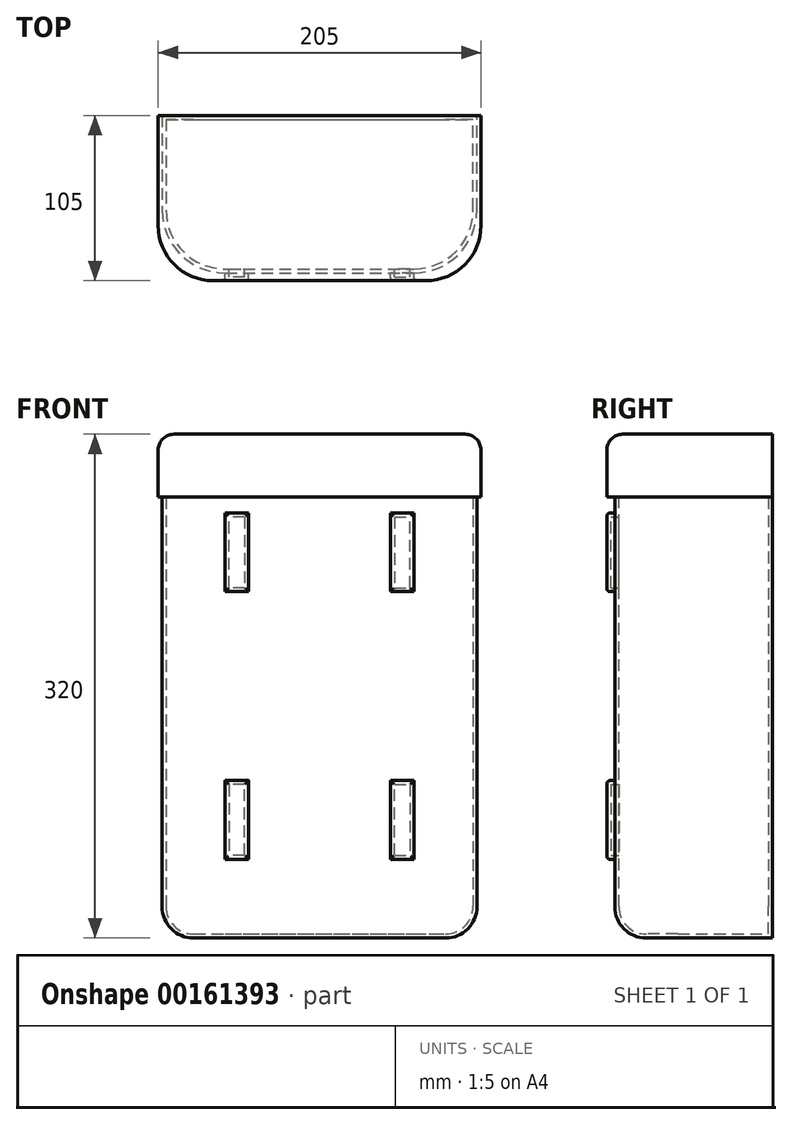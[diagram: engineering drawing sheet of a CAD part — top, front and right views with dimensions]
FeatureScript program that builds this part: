
annotation { "Feature Type Name" : "Feature", "Feature Type Description" : "" }
export const myFeature = defineFeature(function(context is Context, id is Id, definition is map)
    precondition{}
    {
        {
            var Q0;
            Q0=qCreatedBy(makeId("Top.planeOp"),FACE);
            var sketch = newSketch(context, id + "F0", { "sketchPlane" : qUnion([Q0])});
            skLineSegment(sketch, "E0.bottom", {"start": v(-100.73, 42.4) * mm, "end": v(-0.73, 42.4) * mm});
            skLineSegment(sketch, "E0.top", {"start": v(-100.73, -57.6) * mm, "end": v(-0.73, -57.6) * mm});
            skLineSegment(sketch, "E0.left", {"start": v(-100.73, 42.4) * mm, "end": v(-100.73, -57.6) * mm});
            skLineSegment(sketch, "E0.right", {"start": v(-0.73, 42.4) * mm, "end": v(-0.73, -57.6) * mm});
            skSolve(sketch);
        }
        {
            var Q0;
            Q0 = qSketchRegion(id + "F0", true);
            extrude(context, id + "F1", {"entities" : qUnion([Q0]), "depth" : 160 * mm});
        }
        {
            var Q0;
            {var subQ0=makeQuery(id+"F1.opExtrude","SWEPT_FACE",FACE,{"disambiguationData":[OSD([sQuery(id+"F0.wireOp",EDGE,"E0.top")])]});Q0=makeQuery(id+"FtQzAAAF3xHTHlU_1.boolean.opBoolean","MERGE",FACE,{"derivedFrom":[subQ0,makeQuery(id+"FtQzAAAF3xHTHlU_1.opPattern","COPY",FACE,{"derivedFrom":subQ0,"instanceName":"1"})]});}
            var sketch = newSketch(context, id + "F2", { "sketchPlane" : qUnion([Q0])});
            skLineSegment(sketch, "E1.bottom", {"start": v(-60.73, 100) * mm, "end": v(-45.73, 100) * mm});
            skLineSegment(sketch, "E1.top", {"start": v(-60.73, 50) * mm, "end": v(-45.73, 50) * mm});
            skLineSegment(sketch, "E1.left", {"start": v(-60.73, 100) * mm, "end": v(-60.73, 50) * mm});
            skLineSegment(sketch, "E1.right", {"start": v(-45.73, 100) * mm, "end": v(-45.73, 50) * mm});
            skSolve(sketch);
        }
        {
            var Q0;
            Q0 = qSketchRegion(id + "F2", true);
            extrude(context, id + "F3", {"entities" : qUnion([Q0]), "operationType" : NewBodyOperationType.ADD, "depth" : 5 * mm});
        }
        {
            var Q0;
            Q0=makeQuery(id+"F1.opExtrude","SWEPT_BODY",BODY,{"disambiguationData":[OSD([sQuery(id+"F0.wireOp",EDGE,"E0.bottom"),sQuery(id+"F0.wireOp",EDGE,"E0.top"),sQuery(id+"F0.wireOp",EDGE,"E0.left"),sQuery(id+"F0.wireOp",EDGE,"E0.right")])]});
            var Q1;
            Q1=makeQuery(id+"F1.opExtrude","SWEPT_FACE",FACE,{"disambiguationData":[OSD([sQuery(id+"F0.wireOp",EDGE,"E0.right")])]});
            mirror(context, id + "F4", {"operationType" : NewBodyOperationType.ADD, "entities" : qUnion([Q0]), "mirrorPlane" : qUnion([Q1])});
        }
        {
            var Q0;
            Q0=makeQuery(id+"F1.opExtrude","SWEPT_BODY",BODY,{"disambiguationData":[OSD([sQuery(id+"F0.wireOp",EDGE,"E0.bottom"),sQuery(id+"F0.wireOp",EDGE,"E0.top"),sQuery(id+"F0.wireOp",EDGE,"E0.left"),sQuery(id+"F0.wireOp",EDGE,"E0.right")])]});
            var Q1;
            {var subQ0=makeQuery(id+"F1.opExtrude","CAP_FACE",FACE,{"disambiguationData":[OSD([sQuery(id+"F0.wireOp",EDGE,"E0.bottom"),sQuery(id+"F0.wireOp",EDGE,"E0.top"),sQuery(id+"F0.wireOp",EDGE,"E0.left"),sQuery(id+"F0.wireOp",EDGE,"E0.right")])],"isStart":false});Q1=makeQuery(id+"F4.boolean.opBoolean","MERGE",FACE,{"derivedFrom":[subQ0,makeQuery(id+"F4.opPattern","COPY",FACE,{"derivedFrom":subQ0,"instanceName":"1"})]});}
            mirror(context, id + "F5", {"operationType" : NewBodyOperationType.ADD, "entities" : qUnion([Q0]), "mirrorPlane" : qUnion([Q1])});
        }
        {
            var Q0;
            Q0=makeQuery(id+"F5.opPattern","COPY",FACE,{"derivedFrom":makeQuery(id+"F3.opExtrude","CAP_FACE",FACE,{"disambiguationData":[OSD([sQuery(id+"F2.wireOp",EDGE,"E1.bottom"),sQuery(id+"F2.wireOp",EDGE,"E1.top"),sQuery(id+"F2.wireOp",EDGE,"E1.left"),sQuery(id+"F2.wireOp",EDGE,"E1.right")])],"isStart":false}),"instanceName":"1"});
            fillet(context, id + "F6", {"entities" : qUnion([Q0]), "radius" : 2 * mm, "tangentPropagation" : true, "allowEdgeOverflow" : false});
        }
        {
            var Q0;
            Q0=makeQuery(id+"F5.opPattern","COPY",FACE,{"derivedFrom":makeQuery(id+"F4.opPattern","COPY",FACE,{"derivedFrom":makeQuery(id+"F3.opExtrude","CAP_FACE",FACE,{"disambiguationData":[OSD([sQuery(id+"F2.wireOp",EDGE,"E1.bottom"),sQuery(id+"F2.wireOp",EDGE,"E1.top"),sQuery(id+"F2.wireOp",EDGE,"E1.left"),sQuery(id+"F2.wireOp",EDGE,"E1.right")])],"isStart":false}),"instanceName":"1"}),"instanceName":"1"});
            fillet(context, id + "F7", {"entities" : qUnion([Q0]), "radius" : 2 * mm, "tangentPropagation" : true, "allowEdgeOverflow" : false});
        }
        {
            var Q0;
            Q0=makeQuery(id+"F3.opExtrude","CAP_FACE",FACE,{"disambiguationData":[OSD([sQuery(id+"F2.wireOp",EDGE,"E1.bottom"),sQuery(id+"F2.wireOp",EDGE,"E1.top"),sQuery(id+"F2.wireOp",EDGE,"E1.left"),sQuery(id+"F2.wireOp",EDGE,"E1.right")])],"isStart":false});
            var Q1;
            Q1=makeQuery(id+"F4.opPattern","COPY",FACE,{"derivedFrom":makeQuery(id+"F3.opExtrude","CAP_FACE",FACE,{"disambiguationData":[OSD([sQuery(id+"F2.wireOp",EDGE,"E1.bottom"),sQuery(id+"F2.wireOp",EDGE,"E1.top"),sQuery(id+"F2.wireOp",EDGE,"E1.left"),sQuery(id+"F2.wireOp",EDGE,"E1.right")])],"isStart":false}),"instanceName":"1"});
            fillet(context, id + "F8", {"entities" : qUnion([Q0, Q1]), "radius" : 2 * mm, "tangentPropagation" : true, "allowEdgeOverflow" : false});
        }
        {
            var Q0;
            {var subQ0=makeQuery(id+"F1.opExtrude","SWEPT_EDGE",EDGE,{"disambiguationData":[OSD([sQuery(id+"F0.wireOp",EDGE,"E0.top"),sQuery(id+"F0.wireOp",EDGE,"E0.left")])]});Q0=makeQuery(id+"F5.boolean.opBoolean","MERGE",EDGE,{"derivedFrom":[subQ0,makeQuery(id+"F5.opPattern","COPY",EDGE,{"derivedFrom":subQ0,"instanceName":"1"})]});}
            fillet(context, id + "F9", {"entities" : qUnion([Q0]), "radius" : 40 * mm, "tangentPropagation" : true, "allowEdgeOverflow" : false});
        }
        {
            var Q0;
            {var subQ0=makeQuery(id+"F4.opPattern","COPY",EDGE,{"derivedFrom":makeQuery(id+"F1.opExtrude","SWEPT_EDGE",EDGE,{"disambiguationData":[OSD([sQuery(id+"F0.wireOp",EDGE,"E0.top"),sQuery(id+"F0.wireOp",EDGE,"E0.left")])]}),"instanceName":"1"});Q0=makeQuery(id+"F5.boolean.opBoolean","MERGE",EDGE,{"derivedFrom":[subQ0,makeQuery(id+"F5.opPattern","COPY",EDGE,{"derivedFrom":subQ0,"instanceName":"1"})]});}
            fillet(context, id + "F10", {"entities" : qUnion([Q0]), "radius" : 40 * mm, "tangentPropagation" : true, "allowEdgeOverflow" : false});
        }
        {
            var Q0;
            {var subQ0=sQuery(id+"F0.wireOp",EDGE,"E0.left");var subQ1=sQuery(id+"F0.wireOp",EDGE,"E0.top");var subQ2=makeQuery(id+"F1.opExtrude","CAP_FACE",FACE,{"disambiguationData":[OSD([sQuery(id+"F0.wireOp",EDGE,"E0.bottom"),subQ1,subQ0,sQuery(id+"F0.wireOp",EDGE,"E0.right")])],"isStart":true});var subQ3=makeQuery(id+"F1.opExtrude","SWEPT_EDGE",EDGE,{"disambiguationData":[OSD([subQ1,subQ0])]});Q0=makeQuery(id+"F9.opFillet","BLEND_EDGE",EDGE,{"blendedFrom":[makeQuery(id+"F5.boolean.opBoolean","MERGE",EDGE,{"derivedFrom":[subQ3,makeQuery(id+"F5.opPattern","COPY",EDGE,{"derivedFrom":subQ3,"instanceName":"1"})]}),makeQuery(id+"F4.boolean.opBoolean","MERGE",FACE,{"derivedFrom":[subQ2,makeQuery(id+"F4.opPattern","COPY",FACE,{"derivedFrom":subQ2,"instanceName":"1"})]})],"blendedInto":[makeQuery(id+"F4.boolean.opBoolean","MERGE",FACE,{"derivedFrom":[subQ2,makeQuery(id+"F4.opPattern","COPY",FACE,{"derivedFrom":subQ2,"instanceName":"1"})]})]});}
            var Q1;
            {var subQ0=sQuery(id+"F0.wireOp",EDGE,"E0.left");var subQ1=sQuery(id+"F0.wireOp",EDGE,"E0.top");var subQ2=makeQuery(id+"F1.opExtrude","CAP_FACE",FACE,{"disambiguationData":[OSD([sQuery(id+"F0.wireOp",EDGE,"E0.bottom"),subQ1,subQ0,sQuery(id+"F0.wireOp",EDGE,"E0.right")])],"isStart":true});var subQ3=makeQuery(id+"F4.opPattern","COPY",EDGE,{"derivedFrom":makeQuery(id+"F1.opExtrude","SWEPT_EDGE",EDGE,{"disambiguationData":[OSD([subQ1,subQ0])]}),"instanceName":"1"});Q1=makeQuery(id+"F10.opFillet","BLEND_EDGE",EDGE,{"blendedFrom":[makeQuery(id+"F5.boolean.opBoolean","MERGE",EDGE,{"derivedFrom":[subQ3,makeQuery(id+"F5.opPattern","COPY",EDGE,{"derivedFrom":subQ3,"instanceName":"1"})]}),makeQuery(id+"F4.boolean.opBoolean","MERGE",FACE,{"derivedFrom":[subQ2,makeQuery(id+"F4.opPattern","COPY",FACE,{"derivedFrom":subQ2,"instanceName":"1"})]})],"blendedInto":[makeQuery(id+"F4.boolean.opBoolean","MERGE",FACE,{"derivedFrom":[subQ2,makeQuery(id+"F4.opPattern","COPY",FACE,{"derivedFrom":subQ2,"instanceName":"1"})]})]});}
            fillet(context, id + "F11", {"entities" : qUnion([Q0, Q1]), "radius" : 20 * mm, "tangentPropagation" : true, "allowEdgeOverflow" : false});
        }
        {
            var Q0;
            {var subQ0=makeQuery(id+"F1.opExtrude","CAP_FACE",FACE,{"disambiguationData":[OSD([sQuery(id+"F0.wireOp",EDGE,"E0.bottom"),sQuery(id+"F0.wireOp",EDGE,"E0.top"),sQuery(id+"F0.wireOp",EDGE,"E0.left"),sQuery(id+"F0.wireOp",EDGE,"E0.right")])],"isStart":true});Q0=makeQuery(id+"F5.opPattern","COPY",FACE,{"derivedFrom":makeQuery(id+"F4.boolean.opBoolean","MERGE",FACE,{"derivedFrom":[subQ0,makeQuery(id+"F4.opPattern","COPY",FACE,{"derivedFrom":subQ0,"instanceName":"1"})]}),"instanceName":"1"});}
            shell(context, id + "F12", {"entities" : qUnion([Q0]), "thickness" : 2.5 * mm});
        }
        {
            var Q0;
            {var subQ0=makeQuery(id+"F1.opExtrude","CAP_FACE",FACE,{"disambiguationData":[OSD([sQuery(id+"F0.wireOp",EDGE,"E0.bottom"),sQuery(id+"F0.wireOp",EDGE,"E0.top"),sQuery(id+"F0.wireOp",EDGE,"E0.left"),sQuery(id+"F0.wireOp",EDGE,"E0.right")])],"isStart":true});Q0=makeQuery(id+"F5.opPattern","COPY",FACE,{"derivedFrom":makeQuery(id+"F4.boolean.opBoolean","MERGE",FACE,{"derivedFrom":[subQ0,makeQuery(id+"F4.opPattern","COPY",FACE,{"derivedFrom":subQ0,"instanceName":"1"})]}),"instanceName":"1"});}
            var sketch = newSketch(context, id + "F13", { "sketchPlane" : qUnion([Q0])});
            skLineSegment(sketch, "E2.bottom", {"start": v(-103.23, 42.4) * mm, "end": v(101.77, 42.4) * mm});
            skLineSegment(sketch, "E2.top", {"start": v(-103.23, -62.6) * mm, "end": v(101.77, -62.6) * mm});
            skLineSegment(sketch, "E2.left", {"start": v(-103.23, 42.4) * mm, "end": v(-103.23, -62.6) * mm});
            skLineSegment(sketch, "E2.right", {"start": v(101.77, 42.4) * mm, "end": v(101.77, -62.6) * mm});
            skSolve(sketch);
        }
        {
            var Q0;
            Q0 = qSketchRegion(id + "F13", true);
            extrude(context, id + "F14", {"entities" : qUnion([Q0]), "operationType" : NewBodyOperationType.ADD, "oppositeDirection" : true, "depth" : 40 * mm});
        }
        {
            var Q0;
            Q0=makeQuery(id+"F14.opExtrude","SWEPT_EDGE",EDGE,{"disambiguationData":[OSD([sQuery(id+"F13.wireOp",EDGE,"E2.top"),sQuery(id+"F13.wireOp",EDGE,"E2.left")])]});
            fillet(context, id + "F15", {"entities" : qUnion([Q0]), "radius" : 35 * mm, "tangentPropagation" : true, "allowEdgeOverflow" : false});
        }
        {
            var Q0;
            Q0=makeQuery(id+"F14.opExtrude","SWEPT_EDGE",EDGE,{"disambiguationData":[OSD([sQuery(id+"F13.wireOp",EDGE,"E2.top"),sQuery(id+"F13.wireOp",EDGE,"E2.right")])]});
            fillet(context, id + "F16", {"entities" : qUnion([Q0]), "radius" : 35 * mm, "tangentPropagation" : true, "allowEdgeOverflow" : false});
        }
        {
            var Q0;
            Q0=makeQuery(id+"F14.opExtrude","CAP_EDGE",EDGE,{"disambiguationData":[OSD([sQuery(id+"F13.wireOp",EDGE,"E2.top")])],"isStart":true});
            fillet(context, id + "F17", {"entities" : qUnion([Q0]), "radius" : 10 * mm, "tangentPropagation" : true, "allowEdgeOverflow" : false});
        }
    });
